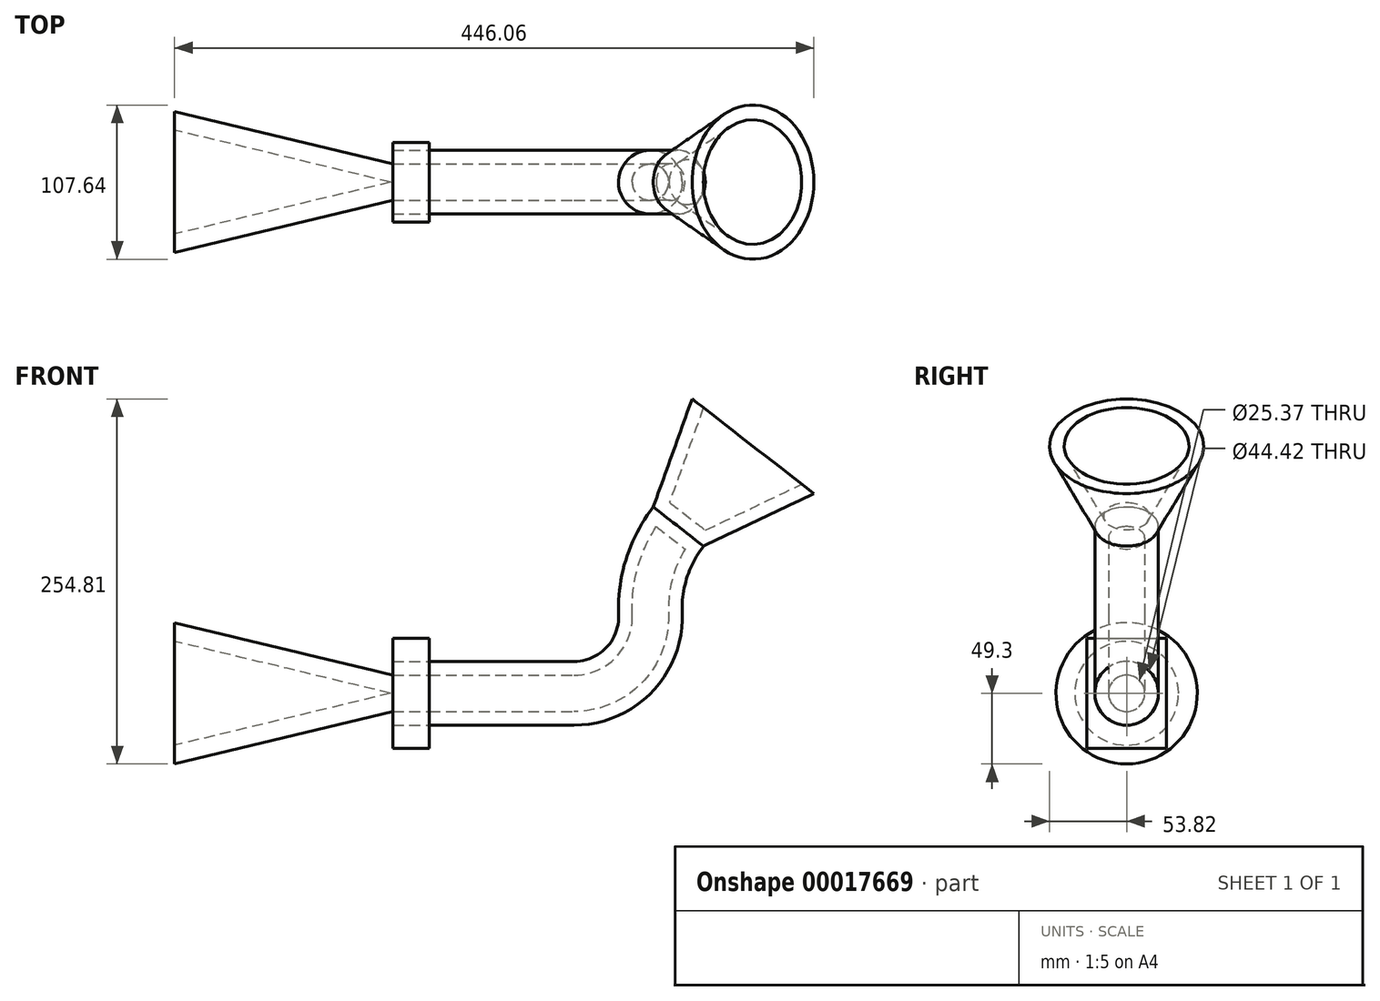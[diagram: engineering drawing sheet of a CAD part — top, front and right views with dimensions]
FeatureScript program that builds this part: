
annotation { "Feature Type Name" : "Feature", "Feature Type Description" : "" }
export const myFeature = defineFeature(function(context is Context, id is Id, definition is map)
    precondition{}
    {
        {
            var Q0;
            Q0=qCreatedBy(makeId("Right.planeOp"),FACE);
            var sketch = newSketch(context, id + "F0", { "sketchPlane" : qUnion([Q0])});
            skCircle(sketch, "E0", {"center": v(0, 0) * mm, "radius": 22.21 * mm});
            skSolve(sketch);
        }
        {
            var Q0;
            Q0=qCreatedBy(makeId("Front.planeOp"),FACE);
            var sketch = newSketch(context, id + "F7", { "sketchPlane" : qUnion([Q0])});
            skLineSegment(sketch, "E1", {"start": v(0, 0) * mm, "end": v(100.87, 0) * mm});
            skArc(sketch, "E2", {"start": v(100.87, 0) * mm, "mid": v(139.35, 16.39) * mm, "end": v(154.2, 55.5) * mm});
            skArc(sketch, "E3", {"start": v(154.2, 55.5) * mm, "mid": v(158.6, 87.67) * mm, "end": v(173.76, 116.39) * mm});
            skSolve(sketch);
        }
        {
            var Q0;
            Q0=makeQuery(id+"F0.imprint","IMPRINT",FACE,{"disambiguationData":[TD([[makeQuery(id+"F0.imprint","IMPRINT",EDGE,{"derivedFrom":sQuery(id+"F0.wireOp",EDGE,"E0")}),1.0]])]});
            var Q1;
            Q1=sQuery(id+"F7.wireOp",EDGE,"E1");
            var Q2;
            Q2=sQuery(id+"F7.wireOp",EDGE,"E2");
            var Q3;
            Q3=sQuery(id+"F7.wireOp",EDGE,"E3");
            sweep(context, id + "F8", {"profiles" : qUnion([Q0]), "path" : qUnion([Q1, Q2, Q3])});
        }
        {
            var Q0;
            Q0=makeQuery(id+"F8.opSweep","CAP_FACE",FACE,{"disambiguationData":[OSD([sQuery(id+"F0.wireOp",EDGE,"E0"),sQuery(id+"F7.wireOp",VERTEX,"E3.end")])],"isStart":false});
            cPlane(context, id + "F1", {"entities" : qUnion([Q0]), "cplaneType" : CPlaneType.OFFSET, "offset" : 76.2 * mm, "width" : 152.4 * mm, "height" : 152.4 * mm});
        }
        {
            var Q0;
            Q0=qCreatedBy(id+"F1.planeOp",FACE);
            var sketch = newSketch(context, id + "F9", { "sketchPlane" : qUnion([Q0])});
            skCircle(sketch, "E4", {"center": v(72.36, 0) * mm, "radius": 53.82 * mm});
            skSolve(sketch);
        }
        {
            var Q0;
            Q0=makeQuery(id+"F9.imprint","IMPRINT",FACE,{"disambiguationData":[TD([[makeQuery(id+"F9.imprint","IMPRINT",EDGE,{"derivedFrom":sQuery(id+"F9.wireOp",EDGE,"E4")}),1.0]])]});
            var Q1;
            Q1=makeQuery(id+"F8.opSweep","CAP_FACE",FACE,{"disambiguationData":[OSD([sQuery(id+"F0.wireOp",EDGE,"E0"),sQuery(id+"F7.wireOp",VERTEX,"E3.end")])],"isStart":false});
            loft(context, id + "F2", {"sheetProfilesArray" : [{ "sheetProfileEntities" : qUnion([Q0]) }, { "sheetProfileEntities" : qUnion([Q1]) }]});
        }
        {
            var Q0;
            Q0=makeQuery(id+"F8.opSweep","CAP_FACE",FACE,{"disambiguationData":[OSD([sQuery(id+"F0.wireOp",EDGE,"E0"),sQuery(id+"F7.wireOp",VERTEX,"E1.start")])],"isStart":true});
            var Q1;
            Q1=makeQuery(id+"F2.opLoft","CAP_FACE",FACE,{"disambiguationData":[OSD([makeQuery(id+"F9.imprint","IMPRINT",FACE,{"disambiguationData":[TD([[makeQuery(id+"F9.imprint","IMPRINT",EDGE,{"derivedFrom":sQuery(id+"F9.wireOp",EDGE,"E4")}),1.0]])]})])],"isStart":true});
            var Q2;
            Q2=makeQuery(id+"F8.opSweep","SWEPT_BODY",BODY,{"disambiguationData":[OSD([sQuery(id+"F0.wireOp",EDGE,"E0"),sQuery(id+"F7.wireOp",EDGE,"E3")])]});
            shell(context, id + "F10", {"entities" : qUnion([Q0, Q1]), "parts" : qUnion([Q2]), "thickness" : 9.52 * mm});
        }
        {
            var Q0;
            Q0=makeQuery(id+"F8.opSweep","CAP_FACE",FACE,{"disambiguationData":[OSD([sQuery(id+"F0.wireOp",EDGE,"E0"),sQuery(id+"F7.wireOp",VERTEX,"E1.start")])],"isStart":true});
            var sketch = newSketch(context, id + "F11", { "sketchPlane" : qUnion([Q0])});
            skLineSegment(sketch, "E5.rect.bottom", {"start": v(27.8, 38.4) * mm, "end": v(-27.8, 38.4) * mm});
            skLineSegment(sketch, "E5.rect.top", {"start": v(27.8, -38.4) * mm, "end": v(-27.8, -38.4) * mm});
            skLineSegment(sketch, "E5.rect.left", {"start": v(27.8, 38.4) * mm, "end": v(27.8, -38.4) * mm});
            skLineSegment(sketch, "E5.rect.right", {"start": v(-27.8, 38.4) * mm, "end": v(-27.8, -38.4) * mm});
            skPoint(sketch, "E5.rect.middle", {"position": v(0, 0) * mm});
            skSolve(sketch);
        }
        {
            var Q0;
            Q0=makeQuery(id+"F11.imprint","IMPRINT",FACE,{"disambiguationData":[TD([[makeQuery(id+"F11.imprint","IMPRINT",EDGE,{"derivedFrom":sQuery(id+"F11.wireOp",EDGE,"E5.rect.bottom")}),1.0]])]});
            var Q1;
            Q1=makeQuery(id+"F11.imprint","IMPRINT",FACE,{"disambiguationData":[TD([[makeQuery(id+"F11.imprint","IMPRINT",EDGE,{"derivedFrom":makeQuery(id+"F10.opShell","OFFSET_EDGE",EDGE,{"disambiguationData":[OSD([sQuery(id+"F0.wireOp",EDGE,"E0"),sQuery(id+"F7.wireOp",VERTEX,"E1.start")])]})}),-1.0]])]});
            extrude(context, id + "F3", {"entities" : qUnion([Q0, Q1]), "operationType" : NewBodyOperationType.ADD, "depth" : 25.4 * mm});
        }
        {
            var Q0;
            Q0=makeQuery(id+"F3.opExtrude","CAP_FACE",FACE,{"disambiguationData":[OSD([sQuery(id+"F0.wireOp",EDGE,"E0"),sQuery(id+"F7.wireOp",VERTEX,"E1.start")])],"isStart":false});
            cPlane(context, id + "F4", {"entities" : qUnion([Q0]), "cplaneType" : CPlaneType.OFFSET, "offset" : 152.4 * mm, "width" : 152.4 * mm, "height" : 152.4 * mm});
        }
        {
            var Q0;
            Q0=qCreatedBy(id+"F4.planeOp",FACE);
            var sketch = newSketch(context, id + "F5", { "sketchPlane" : qUnion([Q0])});
            skCircle(sketch, "E6", {"center": v(0, 0) * mm, "radius": 49.3 * mm});
            skSolve(sketch);
        }
        {
            var Q1;
            Q1=makeQuery(id+"F3.opExtrude","CAP_FACE",FACE,{"disambiguationData":[OSD([sQuery(id+"F0.wireOp",EDGE,"E0"),sQuery(id+"F7.wireOp",VERTEX,"E1.start")])],"isStart":false});
            var Q2;
            Q2=makeQuery(id+"F5.imprint","IMPRINT",FACE,{"disambiguationData":[TD([[makeQuery(id+"F5.imprint","IMPRINT",EDGE,{"derivedFrom":sQuery(id+"F5.wireOp",EDGE,"E6")}),1.0]])]});
            loft(context, id + "F6", {"operationType" : NewBodyOperationType.ADD, "sheetProfilesArray" : [{ "sheetProfileEntities" : qUnion([Q1]) }, { "sheetProfileEntities" : qUnion([Q2]) }]});
        }
        {
            var Q0;
            Q0=makeQuery(id+"F6.opLoft","CAP_FACE",FACE,{"disambiguationData":[OSD([makeQuery(id+"F5.imprint","IMPRINT",FACE,{"disambiguationData":[TD([[makeQuery(id+"F5.imprint","IMPRINT",EDGE,{"derivedFrom":sQuery(id+"F5.wireOp",EDGE,"E6")}),1.0]])]})])],"isStart":true});
            shell(context, id + "F12", {"entities" : qUnion([Q0]), "thickness" : 12.7 * mm});
        }
    });
